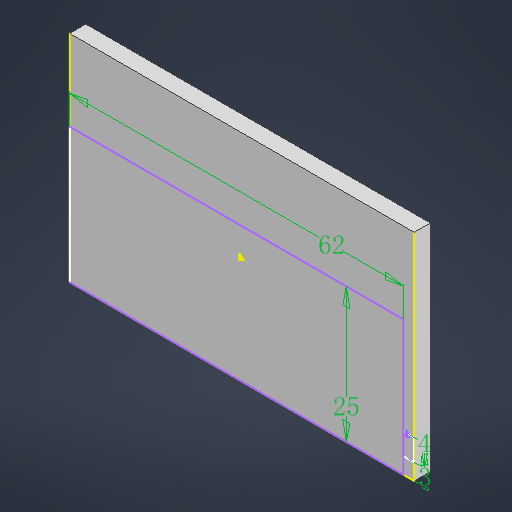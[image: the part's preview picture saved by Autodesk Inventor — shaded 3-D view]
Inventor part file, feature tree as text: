
AUTODESK INVENTOR PART (.ipt)
format: ipt  version: 2025 (Build 290162000, 162)  size: 180,224 bytes
history: native  units: mm
features: sketch x2, extrude x1
ambient origin geometry x8: Origin, YZ Plane, XZ Plane, XY Plane, X Axis, Y Axis, Z Axis, Center Point
bodies: 实体1 (feature_tree)
feature tree (3):
  extrude  "拉伸1"  Depth=40.0mm
  sketch  "草图2"  dims[d2=2.0mm d3=30.0mm d4=3.0mm d5=0.0mm d6=62.0mm d7=4.0mm d8=3.0mm d9=25.0mm]
  sketch  "草图1"  dims[d0=64.0mm d1=40.0mm]
